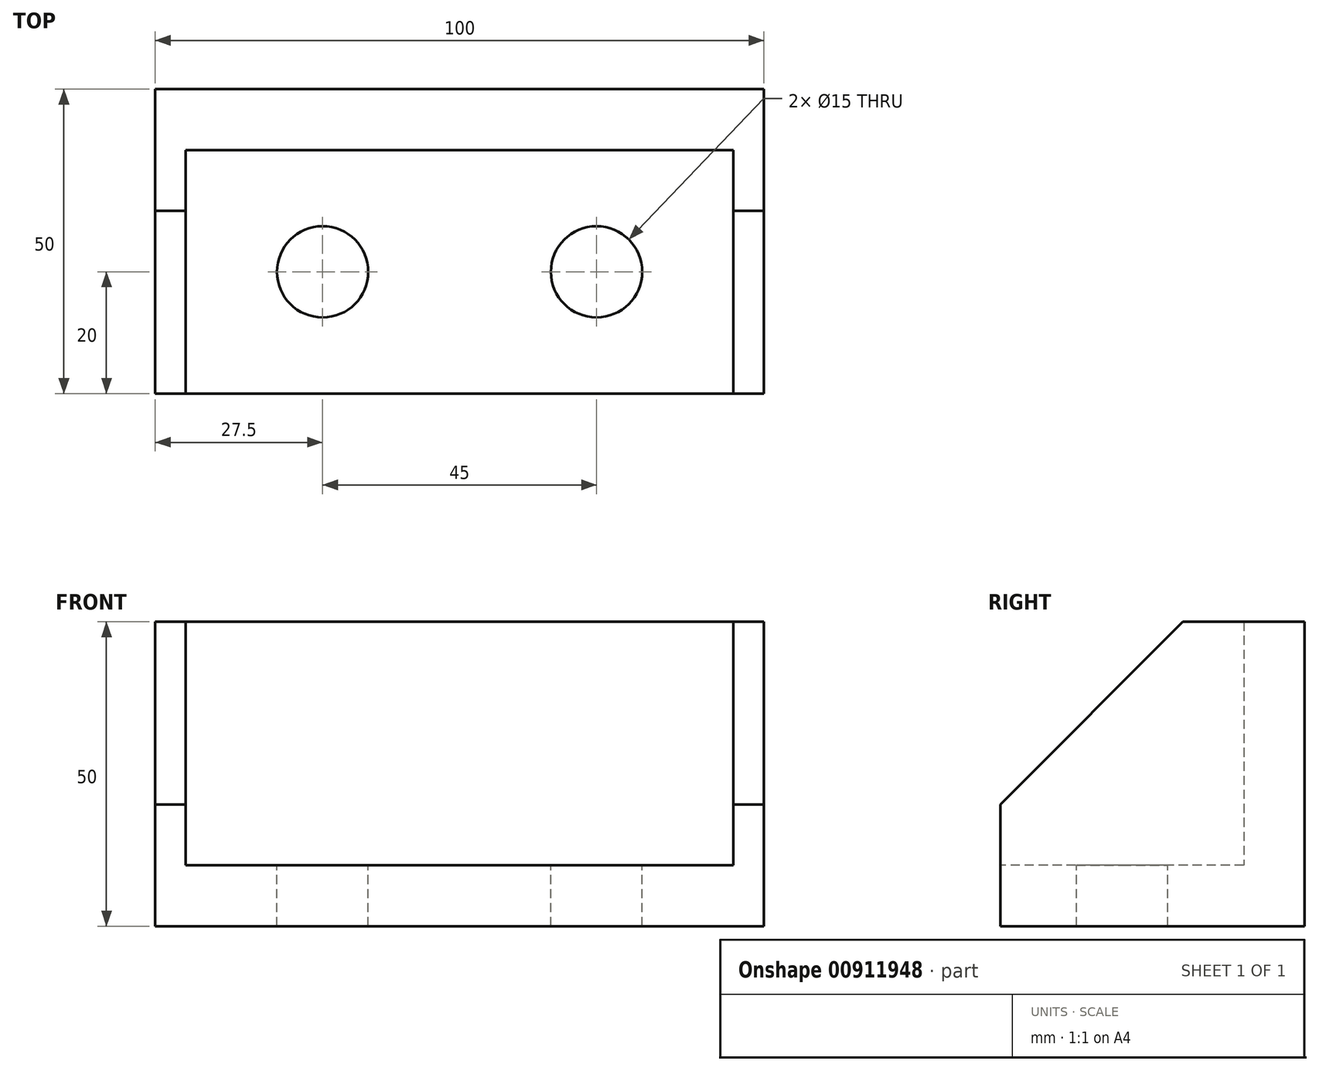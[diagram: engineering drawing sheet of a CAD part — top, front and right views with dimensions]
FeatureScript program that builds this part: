
annotation { "Feature Type Name" : "Feature", "Feature Type Description" : "" }
export const myFeature = defineFeature(function(context is Context, id is Id, definition is map)
    precondition{}
    {
        {
            var Q0;
            Q0=qCreatedBy(makeId("Top.planeOp"),FACE);
            var sketch = newSketch(context, id + "F0", { "sketchPlane" : qUnion([Q0])});
            skLineSegment(sketch, "E0.bottom", {"start": v(0, 0) * mm, "end": v(100, 0) * mm});
            skLineSegment(sketch, "E0.top", {"start": v(0, 50) * mm, "end": v(100, 50) * mm});
            skLineSegment(sketch, "E0.left", {"start": v(0, 0) * mm, "end": v(0, 50) * mm});
            skLineSegment(sketch, "E0.right", {"start": v(100, 0) * mm, "end": v(100, 50) * mm});
            skSolve(sketch);
        }
        {
            var Q0;
            Q0=makeQuery(id+"F0.imprint","IMPRINT",FACE,{"disambiguationData":[TD([[makeQuery(id+"F0.imprint","IMPRINT",EDGE,{"derivedFrom":sQuery(id+"F0.wireOp",EDGE,"E0.bottom")}),1.0]])]});
            extrude(context, id + "F1", {"entities" : qUnion([Q0]), "depth" : 50 * mm, "offsetDistance" : 25 * mm});
        }
        {
            var Q0;
            Q0=makeQuery(id+"F1.opExtrude","CAP_FACE",FACE,{"disambiguationData":[OSD([sQuery(id+"F0.wireOp",EDGE,"E0.bottom"),sQuery(id+"F0.wireOp",EDGE,"E0.top"),sQuery(id+"F0.wireOp",EDGE,"E0.left"),sQuery(id+"F0.wireOp",EDGE,"E0.right")])],"isStart":false});
            var Q1;
            Q1=makeQuery(id+"F1.opExtrude","SWEPT_FACE",FACE,{"disambiguationData":[OSD([sQuery(id+"F0.wireOp",EDGE,"E0.bottom")])]});
            var Q2;
            Q2=makeQuery(id+"F1.opExtrude","SWEPT_FACE",FACE,{"disambiguationData":[OSD([sQuery(id+"F0.wireOp",EDGE,"E0.right")])]});
            var Q3;
            Q3=makeQuery(id+"F1.opExtrude","SWEPT_FACE",FACE,{"disambiguationData":[OSD([sQuery(id+"F0.wireOp",EDGE,"E0.left")])]});
            shell(context, id + "F2", {"entities" : qUnion([Q0, Q1, Q2, Q3]), "thickness" : 10 * mm});
        }
        {
            var Q0;
            Q0=makeQuery(id+"F2.opShell","OFFSET_FACE",FACE,{"disambiguationData":[OSD([sQuery(id+"F0.wireOp",EDGE,"E0.bottom"),sQuery(id+"F0.wireOp",EDGE,"E0.top"),sQuery(id+"F0.wireOp",EDGE,"E0.left"),sQuery(id+"F0.wireOp",EDGE,"E0.right")])]});
            var sketch = newSketch(context, id + "F3", { "sketchPlane" : qUnion([Q0])});
            skLineSegment(sketch, "E1.0", {"start": v(0, 20) * mm, "end": v(100, 20) * mm, "construction": true});
            skLineSegment(sketch, "E2.0", {"start": v(27.5, 0) * mm, "end": v(27.5, 40) * mm, "construction": true});
            skLineSegment(sketch, "E3.0", {"start": v(72.5, 0) * mm, "end": v(72.5, 40) * mm, "construction": true});
            skCircle(sketch, "E4", {"center": v(27.5, 20) * mm, "radius": 7.5 * mm});
            skCircle(sketch, "E5", {"center": v(72.5, 20) * mm, "radius": 7.5 * mm});
            skSolve(sketch);
        }
        {
            var Q0;
            Q0=makeQuery(id+"F3.imprint","IMPRINT",FACE,{"disambiguationData":[TD([[makeQuery(id+"F3.imprint","IMPRINT",EDGE,{"derivedFrom":sQuery(id+"F3.wireOp",EDGE,"E4")}),1.0]])]});
            var Q1;
            Q1=makeQuery(id+"F3.imprint","IMPRINT",FACE,{"disambiguationData":[TD([[makeQuery(id+"F3.imprint","IMPRINT",EDGE,{"derivedFrom":sQuery(id+"F3.wireOp",EDGE,"E5")}),1.0]])]});
            extrude(context, id + "F4", {"entities" : qUnion([Q0, Q1]), "operationType" : NewBodyOperationType.REMOVE, "endBound" : BoundingType.THROUGH_ALL, "oppositeDirection" : true, "depth" : 25 * mm, "offsetDistance" : 25 * mm});
        }
        {
            var Q0;
            Q0=makeQuery(id+"F2.opShell","OFFSET_FACE",FACE,{"disambiguationData":[OSD([sQuery(id+"F0.wireOp",EDGE,"E0.bottom"),sQuery(id+"F0.wireOp",EDGE,"E0.top"),sQuery(id+"F0.wireOp",EDGE,"E0.left"),sQuery(id+"F0.wireOp",EDGE,"E0.right")])]});
            var sketch = newSketch(context, id + "F5", { "sketchPlane" : qUnion([Q0])});
            skLineSegment(sketch, "E6.bottom", {"start": v(0, 40) * mm, "end": v(5, 40) * mm});
            skLineSegment(sketch, "E6.top", {"start": v(0, 0) * mm, "end": v(5, 0) * mm});
            skLineSegment(sketch, "E6.left", {"start": v(0, 40) * mm, "end": v(0, 0) * mm});
            skLineSegment(sketch, "E6.right", {"start": v(5, 40) * mm, "end": v(5, 0) * mm});
            skLineSegment(sketch, "E7.bottom", {"start": v(95, 40) * mm, "end": v(100, 40) * mm});
            skLineSegment(sketch, "E7.top", {"start": v(95, 0) * mm, "end": v(100, 0) * mm});
            skLineSegment(sketch, "E7.left", {"start": v(95, 40) * mm, "end": v(95, 0) * mm});
            skLineSegment(sketch, "E7.right", {"start": v(100, 40) * mm, "end": v(100, 0) * mm});
            skSolve(sketch);
        }
        {
            var Q0;
            Q0=makeQuery(id+"F5.imprint","IMPRINT",FACE,{"disambiguationData":[TD([[makeQuery(id+"F5.imprint","IMPRINT",EDGE,{"derivedFrom":sQuery(id+"F5.wireOp",EDGE,"E6.bottom")}),-1.0]])]});
            var Q1;
            Q1=makeQuery(id+"F5.imprint","IMPRINT",FACE,{"disambiguationData":[TD([[makeQuery(id+"F5.imprint","IMPRINT",EDGE,{"derivedFrom":sQuery(id+"F5.wireOp",EDGE,"E7.bottom")}),-1.0]])]});
            extrude(context, id + "F6", {"entities" : qUnion([Q0, Q1]), "operationType" : NewBodyOperationType.ADD, "depth" : 40 * mm, "offsetDistance" : 25 * mm});
        }
        {
            var Q0;
            Q0=makeQuery(id+"F6.opExtrude","CAP_EDGE",EDGE,{"disambiguationData":[OSD([sQuery(id+"F5.wireOp",EDGE,"E6.top")])],"isStart":false});
            var Q1;
            Q1=makeQuery(id+"F6.opExtrude","CAP_EDGE",EDGE,{"disambiguationData":[OSD([sQuery(id+"F5.wireOp",EDGE,"E7.top")])],"isStart":false});
            chamfer(context, id + "F7", {"entities" : qUnion([Q0, Q1]), "width" : 30 * mm, "tangentPropagation" : true});
        }
    });
